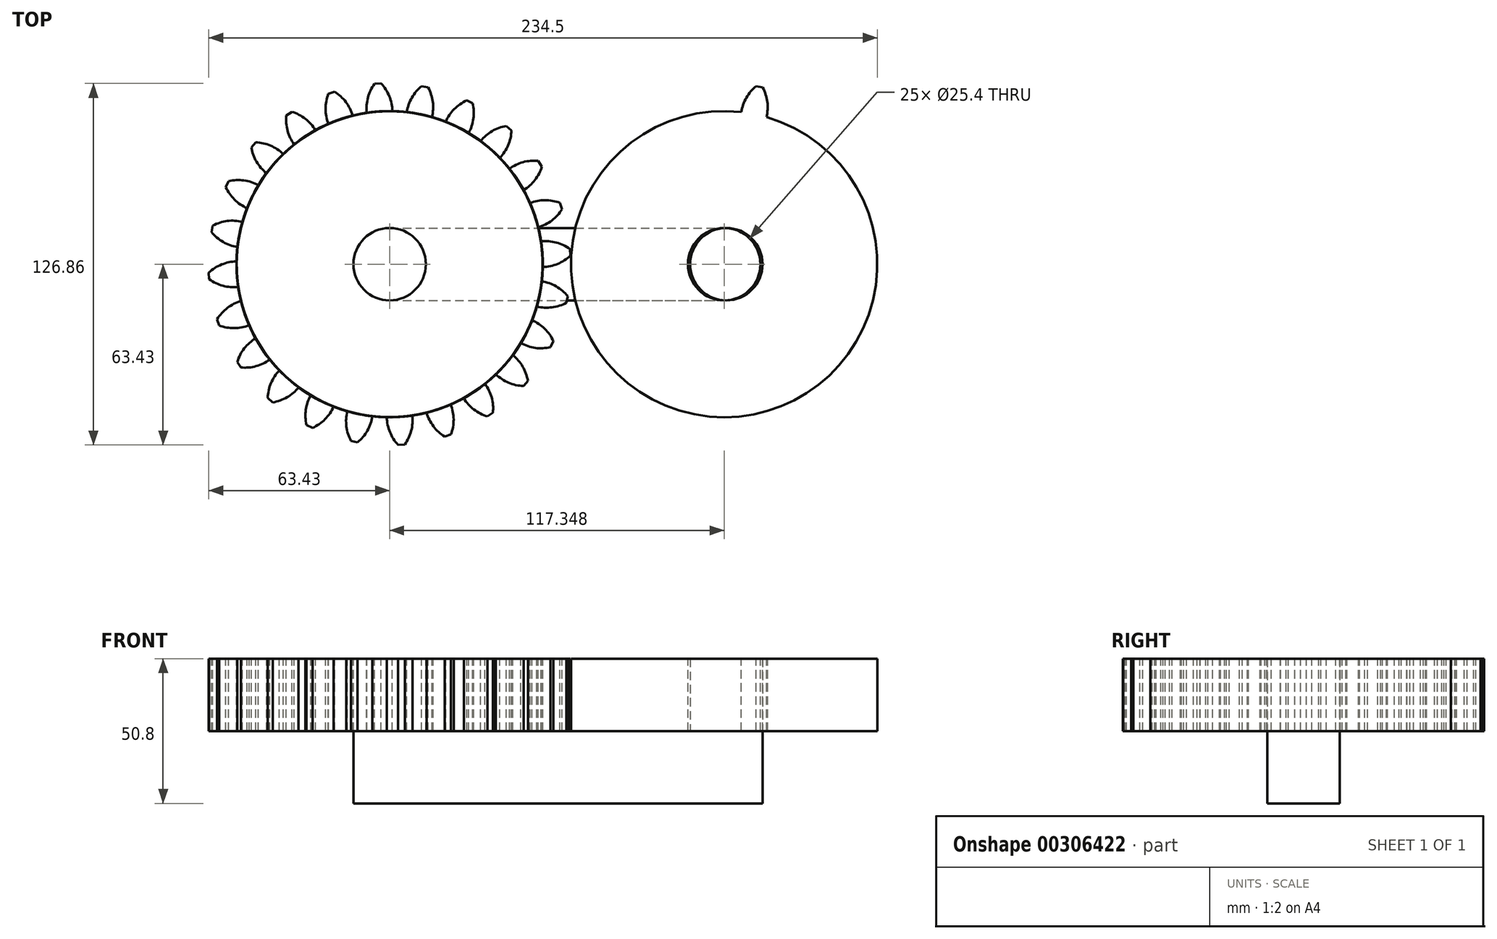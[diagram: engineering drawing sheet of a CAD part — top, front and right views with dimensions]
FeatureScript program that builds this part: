
annotation { "Feature Type Name" : "Feature", "Feature Type Description" : "" }
export const myFeature = defineFeature(function(context is Context, id is Id, definition is map)
    precondition{}
    {
        {
            var Q0;
            Q0=qCreatedBy(makeId("Top.planeOp"),FACE);
            var sketch = newSketch(context, id + "F0", { "sketchPlane" : qUnion([Q0])});
            skLineSegment(sketch, "E0.bottom", {"start": v(0, 0) * mm, "end": v(118.1, 0) * mm});
            skLineSegment(sketch, "E0.top", {"start": v(0, 25.4) * mm, "end": v(118.1, 25.4) * mm});
            skLineSegment(sketch, "E0.left", {"start": v(0, 0) * mm, "end": v(0, 25.4) * mm});
            skLineSegment(sketch, "E0.right", {"start": v(118.11, 0) * mm, "end": v(118.11, 25.4) * mm});
            skCircle(sketch, "E1", {"center": v(0, 12.7) * mm, "radius": 12.7 * mm});
            skCircle(sketch, "E2", {"center": v(118.11, 12.7) * mm, "radius": 12.7 * mm});
            skSolve(sketch);
        }
        {
            var Q0;
            {var subQ0=sQuery(id+"F0.wireOp",EDGE,"E0.left");Q0=makeQuery(id+"F0.imprint","IMPRINT",FACE,{"disambiguationData":[TD([[makeQuery(id+"F0.imprint","IMPRINT",EDGE,{"derivedFrom":subQ0}),1.0]])]});}
            var Q1;
            {var subQ0=sQuery(id+"F0.wireOp",EDGE,"E0.right");Q1=makeQuery(id+"F0.imprint","IMPRINT",FACE,{"disambiguationData":[TD([[makeQuery(id+"F0.imprint","IMPRINT",EDGE,{"derivedFrom":subQ0}),-1.0]])]});}
            var Q2;
            {var subQ0=sQuery(id+"F0.wireOp",EDGE,"E0.left");Q2=makeQuery(id+"F0.imprint","IMPRINT",FACE,{"disambiguationData":[TD([[makeQuery(id+"F0.imprint","IMPRINT",EDGE,{"derivedFrom":subQ0}),-1.0]])]});}
            var Q3;
            {var subQ0=sQuery(id+"F0.wireOp",EDGE,"E0.right");Q3=makeQuery(id+"F0.imprint","IMPRINT",FACE,{"disambiguationData":[TD([[makeQuery(id+"F0.imprint","IMPRINT",EDGE,{"derivedFrom":subQ0}),1.0]])]});}
            var Q4;
            {var subQ0=sQuery(id+"F0.wireOp",EDGE,"E0.bottom");Q4=makeQuery(id+"F0.imprint","IMPRINT",FACE,{"disambiguationData":[TD([[makeQuery(id+"F0.imprint","IMPRINT",EDGE,{"derivedFrom":subQ0}),1.0]])]});}
            extrude(context, id + "F1", {"entities" : qUnion([Q0, Q1, Q2, Q3, Q4]), "depth" : 25.4 * mm});
        }
        {
            var Q0;
            {var subQ0=sQuery(id+"F0.wireOp",EDGE,"E0.left");Q0=makeQuery(id+"F0.imprint","IMPRINT",FACE,{"disambiguationData":[TD([[makeQuery(id+"F0.imprint","IMPRINT",EDGE,{"derivedFrom":subQ0}),-1.0]])]});}
            var Q1;
            {var subQ0=sQuery(id+"F0.wireOp",EDGE,"E0.left");Q1=makeQuery(id+"F0.imprint","IMPRINT",FACE,{"disambiguationData":[TD([[makeQuery(id+"F0.imprint","IMPRINT",EDGE,{"derivedFrom":subQ0}),1.0]])]});}
            var Q2;
            {var subQ0=sQuery(id+"F0.wireOp",EDGE,"E0.right");Q2=makeQuery(id+"F0.imprint","IMPRINT",FACE,{"disambiguationData":[TD([[makeQuery(id+"F0.imprint","IMPRINT",EDGE,{"derivedFrom":subQ0}),-1.0]])]});}
            var Q3;
            {var subQ0=sQuery(id+"F0.wireOp",EDGE,"E0.right");Q3=makeQuery(id+"F0.imprint","IMPRINT",FACE,{"disambiguationData":[TD([[makeQuery(id+"F0.imprint","IMPRINT",EDGE,{"derivedFrom":subQ0}),1.0]])]});}
            extrude(context, id + "F2", {"entities" : qUnion([Q0, Q1, Q2, Q3]), "operationType" : NewBodyOperationType.ADD, "depth" : 50.8 * mm});
        }
        {
            var Q0;
            Q0=makeQuery(id+"F2.opExtrude","CAP_FACE",FACE,{"disambiguationData":[OSD([sQuery(id+"F0.wireOp",EDGE,"E1")])],"isStart":false});
            var sketch = newSketch(context, id + "F3", { "sketchPlane" : qUnion([Q0])});
            skCircle(sketch, "E3", {"center": v(0, 12.7) * mm, "radius": 12.7 * mm});
            skCircle(sketch, "E4", {"center": v(0, 12.7) * mm, "radius": 53.72 * mm});
            skCircle(sketch, "E5", {"center": v(0, 12.7) * mm, "radius": 63.5 * mm, "construction": true});
            skCircle(sketch, "E6", {"center": v(0, 12.7) * mm, "radius": 58.67 * mm, "construction": true});
            skLineSegment(sketch, "E7", {"start": v(0, 12.7) * mm, "end": v(0, 104.9) * mm, "construction": true});
            skCircle(sketch, "E8", {"center": v(0, 12.7) * mm, "radius": 55.14 * mm, "construction": true});
            skCircle(sketch, "E9", {"center": v(0, 71.37) * mm, "radius": 14.6 * mm, "construction": true});
            skLineSegment(sketch, "E10", {"start": v(0, 12.7) * mm, "end": v(-6.02, 104.5) * mm, "construction": true});
            skCircle(sketch, "E11", {"center": v(-13.63, 66.12) * mm, "radius": 14.6 * mm, "construction": true});
            skLineSegment(sketch, "E12", {"start": v(0, 71.37) * mm, "end": v(-124.31, 71.37) * mm, "construction": true});
            skLineSegment(sketch, "E13", {"start": v(0, 71.37) * mm, "end": v(-120.42, 27.54) * mm, "construction": true});
            skArc(sketch, "E14", {"start": v(0, 71.37) * mm, "mid": v(-1.26, 73.9) * mm, "end": v(-2.99, 76.13) * mm});
            skArc(sketch, "E15", {"start": v(0.97, 66.41) * mm, "mid": v(0.7, 68.94) * mm, "end": v(0, 71.37) * mm});
            skArc(sketch, "E16.MirrorCS", {"start": v(-7.66, 70.87) * mm, "mid": v(-6.73, 73.54) * mm, "end": v(-5.32, 75.98) * mm});
            skArc(sketch, "E17.MirrorCS", {"start": v(-7.98, 65.83) * mm, "mid": v(-8.04, 68.36) * mm, "end": v(-7.66, 70.87) * mm});
            skLineSegment(sketch, "E18", {"start": v(-5.32, 75.98) * mm, "end": v(-2.99, 76.13) * mm});
            skSolve(sketch);
        }
        {
            var Q0;
            Q0 = qSketchRegion(id + "F3", true);
            extrude(context, id + "F4", {"entities" : qUnion([Q0]), "oppositeDirection" : true, "depth" : 25.4 * mm});
        }
        {
            var Q0;
            Q0=makeQuery(id+"F4.opExtrude","SWEPT_BODY",BODY,{"disambiguationData":[OSD([sQuery(id+"F3.wireOp",EDGE,"E3"),sQuery(id+"F3.wireOp",EDGE,"E4"),sQuery(id+"F3.wireOp",EDGE,"E14"),sQuery(id+"F3.wireOp",EDGE,"E15"),sQuery(id+"F3.wireOp",EDGE,"E16.MirrorCS"),sQuery(id+"F3.wireOp",EDGE,"E17.MirrorCS"),sQuery(id+"F3.wireOp",EDGE,"E18")])]});
            var Q1;
            Q1=makeQuery(id+"F4.opExtrude","SWEPT_FACE",FACE,{"disambiguationData":[OSD([sQuery(id+"F3.wireOp",EDGE,"E4")])]});
            circularPattern(context, id + "F5", {"entities" : qUnion([Q0]), "axis" : qUnion([Q1]), "angle" : 15 * degree, "instanceCount" : 24});
        }
        {
            var Q0;
            Q0=makeQuery(id+"F5.opPattern","COPY",BODY,{"derivedFrom":makeQuery(id+"F4.opExtrude","SWEPT_BODY",BODY,{"disambiguationData":[OSD([sQuery(id+"F3.wireOp",EDGE,"E3"),sQuery(id+"F3.wireOp",EDGE,"E4"),sQuery(id+"F3.wireOp",EDGE,"E14"),sQuery(id+"F3.wireOp",EDGE,"E15"),sQuery(id+"F3.wireOp",EDGE,"E16.MirrorCS"),sQuery(id+"F3.wireOp",EDGE,"E17.MirrorCS"),sQuery(id+"F3.wireOp",EDGE,"E18")])]}),"instanceName":"23"});
            transform(context, id + "F6", {"entities" : qUnion([Q0]), "transformType" : TransformType.TRANSLATION_3D, "dx" : 117.35 * mm, "dy" : 0 * mm, "dz" : 0 * mm, "makeCopy" : true});
        }
    });
